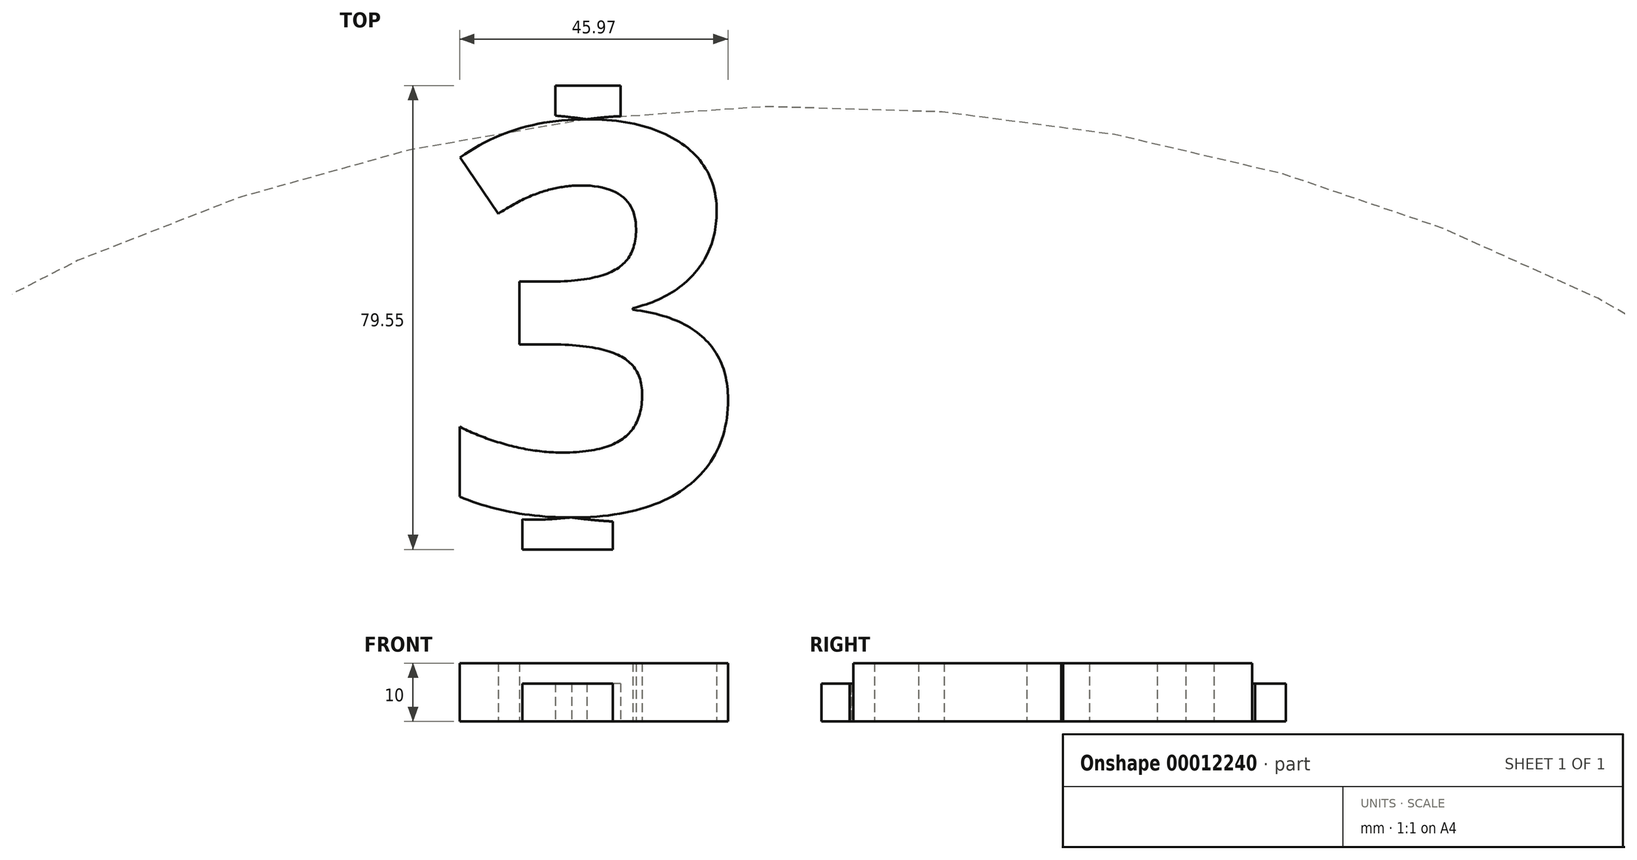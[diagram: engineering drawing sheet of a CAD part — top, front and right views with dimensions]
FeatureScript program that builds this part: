
annotation { "Feature Type Name" : "Feature", "Feature Type Description" : "" }
export const myFeature = defineFeature(function(context is Context, id is Id, definition is map)
    precondition{}
    {
        {
            var Q0;
            Q0=qCreatedBy(makeId("Top.planeOp"),FACE);
            var sketch = newSketch(context, id + "F0", { "sketchPlane" : qUnion([Q0])});
            skText(sketch, "E0", { "text": "3", "fontName": "OpenSans-Bold.ttf"});
            const initialGuessF0  = {"E0": [-0.04952, 0, 1, 0, 0.067]};
            skSetInitialGuess(sketch, initialGuessF0);
            skSolve(sketch);
        }
        {
            var Q0;
            Q0=makeQuery(id+"F0.imprint","IMPRINT",FACE,{"disambiguationData":[TD([[makeQuery(id+"F0.imprint","IMPRINT",EDGE,{"derivedFrom":sQuery(id+"F0.wireOp",EDGE,"E0.sketch_text.stroke-0")}),-1.0]])]});
            extrude(context, id + "F1", {"entities" : qUnion([Q0]), "depth" : 10 * mm});
        }
        {
            var Q0;
            Q0=qCreatedBy(makeId("Top.planeOp"),FACE);
            var sketch = newSketch(context, id + "F2", { "sketchPlane" : qUnion([Q0])});
            skFitSpline(sketch, "E1.0.0", {"points": [v(-5.72, 40.99) * mm, v(-1.95, 45.35) * mm, v(-1.95, 51.57) * mm]});
            skFitSpline(sketch, "E1.0.1", {"points": [v(-1.95, 51.57) * mm, v(-1.95, 59.02) * mm, v(-7.92, 63.2) * mm]});
            skFitSpline(sketch, "E1.0.2", {"points": [v(-7.92, 63.2) * mm, v(-13.9, 67.38) * mm, v(-24.2, 67.38) * mm]});
            skFitSpline(sketch, "E1.0.3", {"points": [v(-24.2, 67.38) * mm, v(-36.8, 67.38) * mm, v(-45.89, 60.84) * mm]});
            skLineSegment(sketch, "E1.0.4", {"start": v(-45.89, 60.84) * mm, "end": v(-39.39, 51.17) * mm});
            skFitSpline(sketch, "E1.0.5", {"points": [v(-39.39, 51.17) * mm, v(-35.26, 53.84) * mm, v(-31.87, 54.93) * mm]});
            skFitSpline(sketch, "E1.0.6", {"points": [v(-31.87, 54.93) * mm, v(-28.48, 56.02) * mm, v(-25.21, 56.02) * mm]});
            skFitSpline(sketch, "E1.0.7", {"points": [v(-25.21, 56.02) * mm, v(-15.76, 56.02) * mm, v(-15.76, 48.48) * mm]});
            skFitSpline(sketch, "E1.0.8", {"points": [v(-15.76, 48.48) * mm, v(-15.76, 43.58) * mm, v(-19.33, 41.56) * mm]});
            skFitSpline(sketch, "E1.0.9", {"points": [v(-19.33, 41.56) * mm, v(-22.9, 39.53) * mm, v(-30.62, 39.53) * mm]});
            skLineSegment(sketch, "E1.0.10", {"start": v(-30.62, 39.53) * mm, "end": v(-35.75, 39.53) * mm});
            skLineSegment(sketch, "E1.0.11", {"start": v(-35.75, 39.53) * mm, "end": v(-35.75, 28.76) * mm});
            skLineSegment(sketch, "E1.0.12", {"start": v(-35.75, 28.76) * mm, "end": v(-30.7, 28.76) * mm});
            skFitSpline(sketch, "E1.0.13", {"points": [v(-30.7, 28.76) * mm, v(-22.35, 28.76) * mm, v(-18.53, 26.8) * mm]});
            skFitSpline(sketch, "E1.0.14", {"points": [v(-18.53, 26.8) * mm, v(-14.71, 24.85) * mm, v(-14.71, 20.18) * mm]});
            skFitSpline(sketch, "E1.0.15", {"points": [v(-14.71, 20.18) * mm, v(-14.71, 14.95) * mm, v(-18.03, 12.58) * mm]});
            skFitSpline(sketch, "E1.0.16", {"points": [v(-18.03, 12.58) * mm, v(-21.34, 10.22) * mm, v(-28.3, 10.22) * mm]});
            skFitSpline(sketch, "E1.0.17", {"points": [v(-28.3, 10.22) * mm, v(-32.85, 10.22) * mm, v(-37.48, 11.45) * mm]});
            skFitSpline(sketch, "E1.0.18", {"points": [v(-37.48, 11.45) * mm, v(-42.12, 12.68) * mm, v(-45.98, 14.63) * mm]});
            skLineSegment(sketch, "E1.0.19", {"start": v(-45.98, 14.63) * mm, "end": v(-45.98, 2.68) * mm});
            skFitSpline(sketch, "E1.0.20", {"points": [v(-45.98, 2.68) * mm, v(-37.61, -0.92) * mm, v(-26.8, -0.92) * mm]});
            skFitSpline(sketch, "E1.0.21", {"points": [v(-26.8, -0.92) * mm, v(-13.9, -0.92) * mm, v(-6.95, 4.43) * mm]});
            skFitSpline(sketch, "E1.0.22", {"points": [v(-6.95, 4.43) * mm, v(0, 9.77) * mm, v(0, 19.35) * mm]});
            skFitSpline(sketch, "E1.0.23", {"points": [v(0, 19.35) * mm, v(0, 25.94) * mm, v(-4.13, 29.83) * mm]});
            skFitSpline(sketch, "E1.0.24", {"points": [v(-4.13, 29.83) * mm, v(-8.26, 33.72) * mm, v(-16.31, 34.72) * mm]});
            skLineSegment(sketch, "E1.0.25", {"start": v(-16.31, 34.72) * mm, "end": v(-16.31, 34.98) * mm});
            skFitSpline(sketch, "E1.0.26", {"points": [v(-16.31, 34.98) * mm, v(-9.5, 36.63) * mm, v(-5.72, 40.99) * mm]});
            skLineSegment(sketch, "E2", {"start": v(-45.98, 2.68) * mm, "end": v(7.73, 2.68) * mm, "construction": true});
            skLineSegment(sketch, "E3", {"start": v(-45.89, 60.84) * mm, "end": v(-45.89, -16.86) * mm, "construction": true});
            skLineSegment(sketch, "E4", {"start": v(-45.89, -16.86) * mm, "end": v(0, -16.86) * mm, "construction": true});
            skLineSegment(sketch, "E5", {"start": v(0, -16.86) * mm, "end": v(0, 71.85) * mm, "construction": true});
            skLineSegment(sketch, "E6", {"start": v(-22.94, -16.86) * mm, "end": v(-22.94, 74.38) * mm, "construction": true});
            skLineSegment(sketch, "E7", {"start": v(-45.89, 0) * mm, "end": v(0, 0) * mm, "construction": true});
            skLineSegment(sketch, "E8.bottom", {"start": v(-22.94, 0) * mm, "end": v(-35.23, 0) * mm});
            skLineSegment(sketch, "E8.top", {"start": v(-22.94, -6.4) * mm, "end": v(-35.23, -6.4) * mm});
            skLineSegment(sketch, "E8.left", {"start": v(-22.94, 0) * mm, "end": v(-22.94, -6.4) * mm});
            skLineSegment(sketch, "E8.right", {"start": v(-35.23, 0) * mm, "end": v(-35.23, -6.4) * mm});
            skLineSegment(sketch, "E9.bottom", {"start": v(-22.94, 0) * mm, "end": v(-19.74, 0) * mm});
            skLineSegment(sketch, "E9.top", {"start": v(-22.94, -6.4) * mm, "end": v(-19.74, -6.4) * mm});
            skLineSegment(sketch, "E9.right", {"start": v(-19.74, 0) * mm, "end": v(-19.74, -6.4) * mm});
            skLineSegment(sketch, "E10", {"start": v(-24.2, 67.38) * mm, "end": v(-45.89, 67.38) * mm, "construction": true});
            skLineSegment(sketch, "E11", {"start": v(-45.89, 67.38) * mm, "end": v(-45.89, 64.5) * mm, "construction": true});
            skLineSegment(sketch, "E12", {"start": v(-24.2, 67.38) * mm, "end": v(0, 67.38) * mm, "construction": true});
            skLineSegment(sketch, "E13", {"start": v(-45.89, 66.85) * mm, "end": v(0, 66.85) * mm, "construction": true});
            skLineSegment(sketch, "E14.bottom", {"start": v(-22.94, 66.85) * mm, "end": v(-29.6, 66.85) * mm});
            skLineSegment(sketch, "E14.top", {"start": v(-22.94, 73.15) * mm, "end": v(-29.6, 73.15) * mm});
            skLineSegment(sketch, "E14.left", {"start": v(-22.94, 66.85) * mm, "end": v(-22.94, 73.15) * mm});
            skLineSegment(sketch, "E14.right", {"start": v(-29.6, 66.85) * mm, "end": v(-29.6, 73.15) * mm});
            skLineSegment(sketch, "E15.bottom", {"start": v(-22.94, 66.85) * mm, "end": v(-18.43, 66.85) * mm});
            skLineSegment(sketch, "E15.top", {"start": v(-22.94, 73.15) * mm, "end": v(-18.43, 73.15) * mm});
            skLineSegment(sketch, "E15.right", {"start": v(-18.43, 66.85) * mm, "end": v(-18.43, 73.15) * mm});
            skSolve(sketch);
        }
        {
            var Q0;
            {var subQ3=sQuery(id+"F2.wireOp",EDGE,"E8.top");Q0=makeQuery(id+"F2.imprint","IMPRINT",FACE,{"disambiguationData":[TD([[makeQuery(id+"F2.imprint","IMPRINT",EDGE,{"derivedFrom":subQ3}),-1.0]])]});}
            var Q1;
            {var subQ3=sQuery(id+"F2.wireOp",EDGE,"E9.top");Q1=makeQuery(id+"F2.imprint","IMPRINT",FACE,{"disambiguationData":[TD([[makeQuery(id+"F2.imprint","IMPRINT",EDGE,{"derivedFrom":subQ3}),1.0]])]});}
            extrude(context, id + "F3", {"entities" : qUnion([Q0, Q1]), "operationType" : NewBodyOperationType.ADD, "depth" : 6.5 * mm});
        }
        {
            var Q0;
            {var subQ3=sQuery(id+"F2.wireOp",EDGE,"E14.top");Q0=makeQuery(id+"F2.imprint","IMPRINT",FACE,{"disambiguationData":[TD([[makeQuery(id+"F2.imprint","IMPRINT",EDGE,{"derivedFrom":subQ3}),1.0]])]});}
            var Q1;
            {var subQ3=sQuery(id+"F2.wireOp",EDGE,"E15.top");Q1=makeQuery(id+"F2.imprint","IMPRINT",FACE,{"disambiguationData":[TD([[makeQuery(id+"F2.imprint","IMPRINT",EDGE,{"derivedFrom":subQ3}),-1.0]])]});}
            extrude(context, id + "F4", {"entities" : qUnion([Q0, Q1]), "operationType" : NewBodyOperationType.ADD, "depth" : 6.5 * mm});
        }
    });
